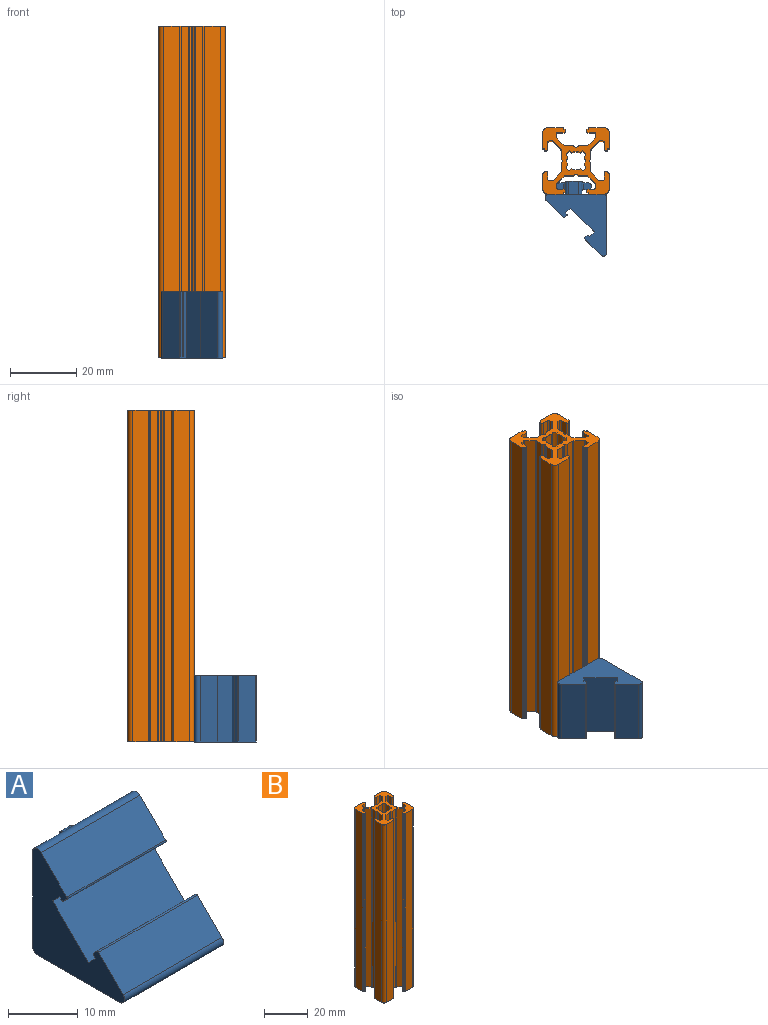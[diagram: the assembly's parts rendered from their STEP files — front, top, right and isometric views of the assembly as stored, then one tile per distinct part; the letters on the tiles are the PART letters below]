
ASSEMBLY  parts=2 mates=1
PART A: 51 faces, bbox 20x22.6x18.6 mm
  f0: plane 20x5.22mm, normal (0,-0.71,0.71), area 147.6mm2, adj f1,f3,f46,f48
  f1: plane 18.59x18.59mm, normal (1,0,0), area 164.1mm2, adj f0,f2,f4,f5,f6,f7,f8,f9
  f2: plane 20x16.59mm, normal (0,1,0), area 302.6mm2, adj f1,f3,f13,f14,f15,f16,f40,f41
  f3: plane 18.59x18.59mm, normal (-1,0,0), area 164.1mm2, adj f0,f2,f4,f5,f6,f7,f8,f9
  f4: plane 20x16.59mm, normal (0,0,-1), area 331.7mm2, adj f1,f3,f44,f45
  f5: plane 20x4.93mm, normal (0,-0.71,0.71), area 139.5mm2, adj f1,f3,f45,f50
  f6: plane 20x0.39mm, normal (0,0.71,-0.71), area 11mm2, adj f1,f3,f8,f49
  f7: plane 20x0.69mm, normal (0,0.71,0.71), area 19.6mm2, adj f1,f3,f49,f50
  f8: plane 20x1.41mm, normal (0,0.71,0.71), area 40mm2, adj f1,f3,f6,f9
  f9: plane 20x7.21mm, normal (0,-0.71,0.71), area 204mm2, adj f1,f3,f8,f10
  f10: plane 20x1.41mm, normal (0,-0.71,-0.71), area 40mm2, adj f1,f3,f9,f11
  f11: plane 20x0.39mm, normal (0,0.71,-0.71), area 11mm2, adj f1,f3,f10,f47
  f12: plane 20x0.69mm, normal (0,-0.71,-0.71), area 19.6mm2, adj f1,f3,f47,f48
  f13: plane 4x3mm, normal (-1,0,0), area 12mm2, adj f2,f17,f40,f43
  f14: plane 4x4mm, normal (0,0,1), area 7mm2, adj f2,f17,f37,f38,f39,f40,f41
  f15: plane 4x3mm, normal (1,0,0), area 12mm2, adj f2,f17,f41,f42
  f16: plane 4x4mm, normal (0,0,-1), area 7mm2, adj f2,f17,f32,f34,f35,f42,f43
  f17: plane 6x5mm, normal (0,1,0), area 29.1mm2, adj f13,f14,f15,f16,f33,f36,f40,f41
  f18: plane 2x1.5mm, normal (0,1,0), area 3mm2, adj f19,f21,f31,f36
  f19: plane 2.3x2mm, normal (-1,0,0), area 4.3mm2, adj f18,f20,f22,f30,f31,f37
  f20: plane 2x1.5mm, normal (0,-1,0), area 3mm2, adj f19,f21,f30,f39
  f21: plane 2.3x2mm, normal (1,0,0), area 4.3mm2, adj f18,f20,f22,f30,f31,f38
  f22: plane 2x0.4mm, normal (0,0,1), area 0.8mm2, adj f19,f21,f30,f31
  f23: plane 2.3x2mm, normal (-1,0,0), area 4.3mm2, adj f24,f26,f27,f28,f29,f32
  f24: plane 2x1.5mm, normal (0,1,0), area 3mm2, adj f23,f25,f28,f33
  f25: plane 2.3x2mm, normal (1,0,0), area 4.3mm2, adj f24,f26,f27,f28,f29,f35
  f26: plane 2x1.5mm, normal (0,-1,0), area 3mm2, adj f23,f25,f29,f34
  f27: plane 2x0.4mm, normal (0,0,-1), area 0.8mm2, adj f23,f25,f28,f29
  f28: cylinder r=0.8mm len=2mm, axis (-1,0,0), area 2.5mm2, adj f23,f24,f25,f27
  f29: cylinder r=0.8mm len=2mm, axis (1,0,0), area 2.5mm2, adj f23,f25,f26,f27
  f30: cylinder r=0.8mm len=2mm, axis (-1,0,0), area 2.5mm2, adj f19,f20,f21,f22
  f31: cylinder r=0.8mm len=2mm, axis (1,0,0), area 2.5mm2, adj f18,f19,f21,f22
  f32: cylinder r=0.5mm len=3mm, axis (0,1,0), area 1.9mm2, adj f16,f23,f33,f34
  f33: cylinder r=0.5mm len=3mm, axis (1,0,0), area 1.9mm2, adj f17,f24,f32,f35
  f34: cylinder r=0.5mm len=3mm, axis (-1,0,0), area 1.9mm2, adj f16,f26,f32,f35
  f35: cylinder r=0.5mm len=3mm, axis (0,-1,0), area 1.9mm2, adj f16,f25,f33,f34
  f36: cylinder r=0.5mm len=3mm, axis (1,0,0), area 1.9mm2, adj f17,f18,f37,f38
  f37: cylinder r=0.5mm len=3mm, axis (0,1,0), area 1.9mm2, adj f14,f19,f36,f39
  f38: cylinder r=0.5mm len=3mm, axis (0,-1,0), area 1.9mm2, adj f14,f21,f36,f39
  f39: cylinder r=0.5mm len=3mm, axis (-1,0,0), area 1.9mm2, adj f14,f20,f37,f38
  f40: cylinder r=1mm len=4mm, axis (0,1,0), area 6.3mm2, adj f2,f13,f14,f17
  f41: cylinder r=1mm len=4mm, axis (0,-1,0), area 6.3mm2, adj f2,f14,f15,f17
  f42: cylinder r=1mm len=4mm, axis (0,1,0), area 6.3mm2, adj f2,f15,f16,f17
  f43: cylinder r=1mm len=4mm, axis (0,-1,0), area 6.3mm2, adj f2,f13,f16,f17
  f44: cylinder r=1mm len=20mm, axis (-1,0,0), area 31.4mm2, adj f1,f2,f3,f4
  f45: cylinder r=1mm len=20mm, axis (-1,0,0), area 47.1mm2, adj f1,f3,f4,f5
  f46: cylinder r=1mm len=20mm, axis (-1,0,0), area 47.1mm2, adj f0,f1,f2,f3
  f47: cylinder r=0.25mm len=20mm, axis (1,0,0), area 7.9mm2, adj f1,f3,f11,f12
  f48: cylinder r=0.25mm len=20mm, axis (-1,0,0), area 7.9mm2, adj f0,f1,f3,f12
  f49: cylinder r=0.25mm len=20mm, axis (1,0,0), area 7.9mm2, adj f1,f3,f6,f7
  f50: cylinder r=0.25mm len=20mm, axis (1,0,0), area 7.9mm2, adj f1,f3,f5,f7
PART B: 154 faces, bbox 20x20x100 mm
  f0: cylinder r=3.55mm len=100mm, axis (0,0,1), area 153.8mm2, adj f1,f151,f152,f153
  f1: plane 100x0.65mm, normal (0.77,0.64,0), area 85.1mm2, adj f0,f2,f152,f153
  f2: cylinder r=2.75mm len=100mm, axis (0,0,1), area 261.4mm2, adj f1,f3,f152,f153
  f3: plane 100x0.65mm, normal (0.77,-0.64,0), area 85.1mm2, adj f2,f4,f152,f153
  f4: cylinder r=3.55mm len=100mm, axis (0,0,1), area 153.8mm2, adj f3,f5,f152,f153
  f5: plane 100x0.66mm, normal (-0.64,0.77,0), area 85.2mm2, adj f4,f6,f152,f153
  f6: cylinder r=2.75mm len=100mm, axis (0,0,1), area 261.4mm2, adj f5,f7,f152,f153
  f7: plane 100x0.66mm, normal (0.64,0.77,0), area 85.2mm2, adj f6,f8,f152,f153
  f8: cylinder r=3.55mm len=100mm, axis (0,0,1), area 153.8mm2, adj f7,f9,f152,f153
  f9: plane 100x0.65mm, normal (-0.77,-0.64,0), area 85.1mm2, adj f8,f10,f152,f153
  f10: cylinder r=2.75mm len=100mm, axis (0,0,1), area 261.4mm2, adj f9,f11,f152,f153
  f11: plane 100x0.65mm, normal (-0.77,0.64,0), area 85.1mm2, adj f10,f12,f152,f153
  f12: cylinder r=3.55mm len=100mm, axis (0,0,1), area 153.8mm2, adj f11,f13,f152,f153
  f13: plane 100x0.66mm, normal (0.64,-0.77,0), area 85.2mm2, adj f12,f14,f152,f153
  f14: cylinder r=2.75mm len=100mm, axis (0,0,1), area 261.4mm2, adj f13,f151,f152,f153
  f15: cylinder r=1.5mm len=100mm, axis (0,0,1), area 235.6mm2, adj f16,f150,f152,f153
  f16: plane 100x4.65mm, normal (0,1,0), area 465mm2, adj f15,f17,f152,f153
  f17: cylinder r=0.2mm len=100mm, axis (0,0,1), area 31.4mm2, adj f16,f18,f152,f153
  f18: plane 100x0.3mm, normal (1,0,0), area 30mm2, adj f17,f19,f152,f153
  f19: plane 100x0.35mm, normal (0,1,0), area 35mm2, adj f18,f20,f152,f153
  f20: cylinder r=0.2mm len=100mm, axis (0,0,1), area 31.4mm2, adj f19,f21,f152,f153
  f21: plane 100x0.3mm, normal (1,0,0), area 30mm2, adj f20,f22,f152,f153
  f22: cylinder r=0.5mm len=100mm, axis (0,0,1), area 78.5mm2, adj f21,f23,f152,f153
  f23: plane 100x1.9mm, normal (0,-1,0), area 190mm2, adj f22,f24,f152,f153
  f24: cylinder r=0.5mm len=100mm, axis (0,0,1), area 78.5mm2, adj f23,f25,f152,f153
  f25: plane 100x0.73mm, normal (1,0,0), area 73.2mm2, adj f24,f26,f152,f153
  f26: cylinder r=0.5mm len=100mm, axis (0,0,1), area 39.3mm2, adj f25,f27,f152,f153
  f27: plane 100x2.27mm, normal (0.71,0.71,0), area 320.7mm2, adj f26,f28,f152,f153
  f28: cylinder r=0.5mm len=100mm, axis (0,0,1), area 39.3mm2, adj f27,f29,f152,f153
  f29: plane 100x2.28mm, normal (0,1,0), area 227.9mm2, adj f28,f30,f152,f153
  f30: cylinder r=0.2mm len=100mm, axis (0,0,1), area 10.5mm2, adj f29,f31,f152,f153
  f31: plane 100x0.75mm, normal (0.5,0.87,0), area 87mm2, adj f30,f32,f152,f153
  f32: cylinder r=0.2mm len=100mm, axis (0,0,1), area 20.9mm2, adj f31,f33,f152,f153
  f33: plane 100x0.75mm, normal (-0.5,0.87,0), area 87mm2, adj f32,f34,f152,f153
  f34: cylinder r=0.2mm len=100mm, axis (0,0,1), area 10.5mm2, adj f33,f35,f152,f153
  f35: plane 100x2.28mm, normal (0,1,0), area 227.9mm2, adj f34,f36,f152,f153
  f36: cylinder r=0.5mm len=100mm, axis (0,0,1), area 39.3mm2, adj f35,f37,f152,f153
  f37: plane 100x2.27mm, normal (-0.71,0.71,0), area 320.7mm2, adj f36,f38,f152,f153
  f38: cylinder r=0.5mm len=100mm, axis (0,0,1), area 39.3mm2, adj f37,f39,f152,f153
  f39: plane 100x0.73mm, normal (-1,0,0), area 73.2mm2, adj f38,f40,f152,f153
  f40: cylinder r=0.5mm len=100mm, axis (0,0,1), area 78.5mm2, adj f39,f41,f152,f153
  f41: plane 100x1.9mm, normal (0,-1,0), area 190mm2, adj f40,f42,f152,f153
  f42: cylinder r=0.5mm len=100mm, axis (0,0,1), area 78.5mm2, adj f41,f43,f152,f153
  f43: plane 100x0.3mm, normal (-1,0,0), area 30mm2, adj f42,f44,f152,f153
  f44: cylinder r=0.2mm len=100mm, axis (0,0,1), area 31.4mm2, adj f43,f45,f152,f153
  f45: plane 100x0.35mm, normal (0,1,0), area 35mm2, adj f44,f46,f152,f153
  f46: plane 100x0.3mm, normal (-1,0,0), area 30mm2, adj f45,f47,f152,f153
  f47: cylinder r=0.2mm len=100mm, axis (0,0,1), area 31.4mm2, adj f46,f48,f152,f153
  f48: plane 100x4.65mm, normal (0,1,0), area 465mm2, adj f47,f49,f152,f153
  f49: cylinder r=1.5mm len=100mm, axis (0,0,1), area 235.6mm2, adj f48,f50,f152,f153
  f50: plane 100x4.65mm, normal (1,0,0), area 465mm2, adj f49,f51,f152,f153
  f51: cylinder r=0.2mm len=100mm, axis (0,0,1), area 31.4mm2, adj f50,f52,f152,f153
  f52: plane 100x0.3mm, normal (0,-1,0), area 30mm2, adj f51,f53,f152,f153
  f53: plane 100x0.35mm, normal (1,0,0), area 35mm2, adj f52,f54,f152,f153
  f54: cylinder r=0.2mm len=100mm, axis (0,0,1), area 31.4mm2, adj f53,f55,f152,f153
  f55: plane 100x0.3mm, normal (0,-1,0), area 30mm2, adj f54,f56,f152,f153
  f56: cylinder r=0.5mm len=100mm, axis (0,0,1), area 78.5mm2, adj f55,f57,f152,f153
  f57: plane 100x1.9mm, normal (-1,0,0), area 190mm2, adj f56,f58,f152,f153
  f58: cylinder r=0.5mm len=100mm, axis (0,0,1), area 78.5mm2, adj f57,f59,f152,f153
  f59: plane 100x0.73mm, normal (0,-1,0), area 73.2mm2, adj f58,f60,f152,f153
  f60: cylinder r=0.5mm len=100mm, axis (0,0,1), area 39.3mm2, adj f59,f61,f152,f153
  f61: plane 100x2.27mm, normal (0.71,-0.71,0), area 320.7mm2, adj f60,f62,f152,f153
  f62: cylinder r=0.5mm len=100mm, axis (0,0,1), area 39.3mm2, adj f61,f63,f152,f153
  f63: plane 100x2.28mm, normal (1,0,0), area 227.9mm2, adj f62,f64,f152,f153
  f64: cylinder r=0.2mm len=100mm, axis (0,0,1), area 10.5mm2, adj f63,f65,f152,f153
  f65: plane 100x0.75mm, normal (0.87,-0.5,0), area 87mm2, adj f64,f66,f152,f153
  f66: cylinder r=0.2mm len=100mm, axis (0,0,1), area 20.9mm2, adj f65,f67,f152,f153
  f67: plane 100x0.75mm, normal (0.87,0.5,0), area 87mm2, adj f66,f68,f152,f153
  f68: cylinder r=0.2mm len=100mm, axis (0,0,1), area 10.5mm2, adj f67,f69,f152,f153
  f69: plane 100x2.28mm, normal (1,0,0), area 227.9mm2, adj f68,f70,f152,f153
  f70: cylinder r=0.5mm len=100mm, axis (0,0,1), area 39.3mm2, adj f69,f71,f152,f153
  f71: plane 100x2.27mm, normal (0.71,0.71,0), area 320.7mm2, adj f70,f72,f152,f153
  f72: cylinder r=0.5mm len=100mm, axis (0,0,1), area 39.3mm2, adj f71,f73,f152,f153
  f73: plane 100x0.73mm, normal (0,1,0), area 73.2mm2, adj f72,f74,f152,f153
  f74: cylinder r=0.5mm len=100mm, axis (0,0,1), area 78.5mm2, adj f73,f75,f152,f153
  f75: plane 100x1.9mm, normal (-1,0,0), area 190mm2, adj f74,f76,f152,f153
  f76: cylinder r=0.5mm len=100mm, axis (0,0,1), area 78.5mm2, adj f75,f77,f152,f153
  f77: plane 100x0.3mm, normal (0,1,0), area 30mm2, adj f76,f78,f152,f153
  f78: cylinder r=0.2mm len=100mm, axis (0,0,1), area 31.4mm2, adj f77,f79,f152,f153
  f79: plane 100x0.35mm, normal (1,0,0), area 35mm2, adj f78,f80,f152,f153
  f80: plane 100x0.3mm, normal (0,1,0), area 30mm2, adj f79,f81,f152,f153
  f81: cylinder r=0.2mm len=100mm, axis (0,0,1), area 31.4mm2, adj f80,f82,f152,f153
  f82: plane 100x4.65mm, normal (1,0,0), area 465mm2, adj f81,f83,f152,f153
  f83: cylinder r=1.5mm len=100mm, axis (0,0,1), area 235.6mm2, adj f82,f84,f152,f153
  f84: plane 100x4.65mm, normal (0,-1,0), area 465mm2, adj f83,f85,f152,f153
  f85: cylinder r=0.2mm len=100mm, axis (0,0,1), area 31.4mm2, adj f84,f86,f152,f153
  f86: plane 100x0.3mm, normal (-1,0,0), area 30mm2, adj f85,f87,f152,f153
  f87: plane 100x0.35mm, normal (0,-1,0), area 35mm2, adj f86,f88,f152,f153
  f88: cylinder r=0.2mm len=100mm, axis (0,0,1), area 31.4mm2, adj f87,f89,f152,f153
  f89: plane 100x0.3mm, normal (-1,0,0), area 30mm2, adj f88,f90,f152,f153
  f90: cylinder r=0.5mm len=100mm, axis (0,0,1), area 78.5mm2, adj f89,f91,f152,f153
  f91: plane 100x1.9mm, normal (0,1,0), area 190mm2, adj f90,f92,f152,f153
  f92: cylinder r=0.5mm len=100mm, axis (0,0,1), area 78.5mm2, adj f91,f93,f152,f153
  f93: plane 100x0.73mm, normal (-1,0,0), area 73.2mm2, adj f92,f94,f152,f153
  f94: cylinder r=0.5mm len=100mm, axis (0,0,1), area 39.3mm2, adj f93,f95,f152,f153
  f95: plane 100x2.27mm, normal (-0.71,-0.71,0), area 320.7mm2, adj f94,f96,f152,f153
  f96: cylinder r=0.5mm len=100mm, axis (0,0,1), area 39.3mm2, adj f95,f97,f152,f153
  f97: plane 100x2.28mm, normal (0,-1,0), area 227.9mm2, adj f96,f98,f152,f153
  f98: cylinder r=0.2mm len=100mm, axis (0,0,1), area 10.5mm2, adj f97,f99,f152,f153
  f99: plane 100x0.75mm, normal (-0.5,-0.87,0), area 87mm2, adj f98,f100,f152,f153
  f100: cylinder r=0.2mm len=100mm, axis (0,0,1), area 20.9mm2, adj f99,f101,f152,f153
  f101: plane 100x0.75mm, normal (0.5,-0.87,0), area 87mm2, adj f100,f102,f152,f153
  f102: cylinder r=0.2mm len=100mm, axis (0,0,1), area 10.5mm2, adj f101,f103,f152,f153
  f103: plane 100x2.28mm, normal (0,-1,0), area 227.9mm2, adj f102,f104,f152,f153
  f104: cylinder r=0.5mm len=100mm, axis (0,0,1), area 39.3mm2, adj f103,f105,f152,f153
  f105: plane 100x2.27mm, normal (0.71,-0.71,0), area 320.7mm2, adj f104,f106,f152,f153
  f106: cylinder r=0.5mm len=100mm, axis (0,0,1), area 39.3mm2, adj f105,f107,f152,f153
  f107: plane 100x0.73mm, normal (1,0,0), area 73.2mm2, adj f106,f108,f152,f153
  f108: cylinder r=0.5mm len=100mm, axis (0,0,1), area 78.5mm2, adj f107,f109,f152,f153
  f109: plane 100x1.9mm, normal (0,1,0), area 190mm2, adj f108,f110,f152,f153
  f110: cylinder r=0.5mm len=100mm, axis (0,0,1), area 78.5mm2, adj f109,f111,f152,f153
  f111: plane 100x0.3mm, normal (1,0,0), area 30mm2, adj f110,f112,f152,f153
  f112: cylinder r=0.2mm len=100mm, axis (0,0,1), area 31.4mm2, adj f111,f113,f152,f153
  f113: plane 100x0.35mm, normal (0,-1,0), area 35mm2, adj f112,f114,f152,f153
  f114: plane 100x0.3mm, normal (1,0,0), area 30mm2, adj f113,f115,f152,f153
  f115: cylinder r=0.2mm len=100mm, axis (0,0,1), area 31.4mm2, adj f114,f116,f152,f153
  f116: plane 100x4.65mm, normal (0,-1,0), area 465mm2, adj f115,f117,f152,f153
  f117: cylinder r=1.5mm len=100mm, axis (0,0,1), area 235.6mm2, adj f116,f118,f152,f153
  f118: plane 100x4.65mm, normal (-1,0,0), area 465mm2, adj f117,f119,f152,f153
  f119: cylinder r=0.2mm len=100mm, axis (0,0,1), area 31.4mm2, adj f118,f120,f152,f153
  f120: plane 100x0.3mm, normal (0,1,0), area 30mm2, adj f119,f121,f152,f153
  f121: plane 100x0.35mm, normal (-1,0,0), area 35mm2, adj f120,f122,f152,f153
  f122: cylinder r=0.2mm len=100mm, axis (0,0,1), area 31.4mm2, adj f121,f123,f152,f153
  f123: plane 100x0.3mm, normal (0,1,0), area 30mm2, adj f122,f124,f152,f153
  f124: cylinder r=0.5mm len=100mm, axis (0,0,1), area 78.5mm2, adj f123,f125,f152,f153
  f125: plane 100x1.9mm, normal (1,0,0), area 190mm2, adj f124,f126,f152,f153
  f126: cylinder r=0.5mm len=100mm, axis (0,0,1), area 78.5mm2, adj f125,f127,f152,f153
  f127: plane 100x0.73mm, normal (0,1,0), area 73.2mm2, adj f126,f128,f152,f153
  f128: cylinder r=0.5mm len=100mm, axis (0,0,1), area 39.3mm2, adj f127,f129,f152,f153
  f129: plane 100x2.27mm, normal (-0.71,0.71,0), area 320.7mm2, adj f128,f130,f152,f153
  f130: cylinder r=0.5mm len=100mm, axis (0,0,1), area 39.3mm2, adj f129,f131,f152,f153
  f131: plane 100x2.28mm, normal (-1,0,0), area 227.9mm2, adj f130,f132,f152,f153
  f132: cylinder r=0.2mm len=100mm, axis (0,0,1), area 10.5mm2, adj f131,f133,f152,f153
  f133: plane 100x0.75mm, normal (-0.87,0.5,0), area 87mm2, adj f132,f134,f152,f153
  f134: cylinder r=0.2mm len=100mm, axis (0,0,1), area 20.9mm2, adj f133,f135,f152,f153
  f135: plane 100x0.75mm, normal (-0.87,-0.5,0), area 87mm2, adj f134,f136,f152,f153
  f136: cylinder r=0.2mm len=100mm, axis (0,0,1), area 10.5mm2, adj f135,f137,f152,f153
  f137: plane 100x2.28mm, normal (-1,0,0), area 227.9mm2, adj f136,f138,f152,f153
  f138: cylinder r=0.5mm len=100mm, axis (0,0,1), area 39.3mm2, adj f137,f139,f152,f153
  f139: plane 100x2.27mm, normal (-0.71,-0.71,0), area 320.7mm2, adj f138,f140,f152,f153
  f140: cylinder r=0.5mm len=100mm, axis (0,0,1), area 39.3mm2, adj f139,f141,f152,f153
  f141: plane 100x0.73mm, normal (0,-1,0), area 73.2mm2, adj f140,f142,f152,f153
  f142: cylinder r=0.5mm len=100mm, axis (0,0,1), area 78.5mm2, adj f141,f143,f152,f153
  f143: plane 100x1.9mm, normal (1,0,0), area 190mm2, adj f142,f144,f152,f153
  f144: cylinder r=0.5mm len=100mm, axis (0,0,1), area 78.5mm2, adj f143,f145,f152,f153
  f145: plane 100x0.3mm, normal (0,-1,0), area 30mm2, adj f144,f146,f152,f153
  f146: cylinder r=0.2mm len=100mm, axis (0,0,1), area 31.4mm2, adj f145,f147,f152,f153
  f147: plane 100x0.35mm, normal (-1,0,0), area 35mm2, adj f146,f148,f152,f153
  f148: plane 100x0.3mm, normal (0,-1,0), area 30mm2, adj f147,f149,f152,f153
  f149: cylinder r=0.2mm len=100mm, axis (0,0,1), area 31.4mm2, adj f148,f150,f152,f153
  f150: plane 100x4.65mm, normal (-1,0,0), area 465mm2, adj f15,f149,f152,f153
  f151: plane 100x0.66mm, normal (-0.64,-0.77,0), area 85.2mm2, adj f0,f14,f152,f153
  f152: plane 20x20mm, normal (0,0,-1), area 162mm2, adj f0,f1,f2,f3,f4,f5,f6,f7
  f153: plane 20x20mm, normal (0,0,1), area 162mm2, adj f0,f1,f2,f3,f4,f5,f6,f7
PLACE A rot(axis=(0,-1,0),90deg) t=(17.79,-10,-90)mm
PLACE B at identity
MATE fastened A.f3 <-> B.f152  axis (0,0,-1) through (8.5,0,-100)mm
